# Revit family: Sink-Bathroom_Vessel-KOHLER-Sartorial-K-75749
name_source: partatom
category: Plumbing Fixtures
revit_build: Autodesk Revit 2015 (Build: 20140606_1530(x64)
units: mm (PartAtom-declared; Revit-internal decimal feet)

## types (4) — shared parameters
ADA Compliant = Yes
Assembly Code = D2010400
CW Connection = No
Cold Water Inlet = Cold Water Inlet
Date Modified = 11/19/2018
Default Elevation = 34"
Drain Included = No
HW Connection = No
Height = 6 1/8"
Hot Water Inlet = Hot Water Inlet
Length = 21 1/8"
Manufacturer = KOHLER Co.
MasterFormat 1995 = 15410
MasterFormat 2004 = 22.41.16
Material = Vitreous China
Product Documentation Link = http://www.us.kohler.com
Product Name = Sartorial
Product Page URL = http://www.us.kohler.com
URL = https://www.us.kohler.com
Vent Connection = No
Waste Connection = Yes
Waste Water Outlet = Waste Water Outlet
Width = 14 9/16"

## per-type parameters (varying)
| type | Description | Finish | Model | Type |
| Herringbone, 0-White | Herringbone in White on Carillon Rectangle Wading Pool bathroom sink | Kohler-Vitreous_China-0-White | K-75749-HD1-0 | 1 |
| Paisley, 0-White | Paisley in White on Carillon Rectangle Wading Pool bathroom sink | Kohler-Vitreous_China-0-White | K-75749-FP1-0 | 2 |
| Paisley, 7-Black Black | Paisley in Black Black on Carillon Rectangle Wading Pool bathroom sink | Kohler-Vitreous_China-7-Black_Black | K-75749-FP2-7 | 3 |
| Herringbone, 7-Black Black | Herringbone in Black Black on Carillon Rectangle Wading Pool bathroom sink | Kohler-Vitreous_China-7-Black_Black | K-75749-HD2-7 | 4 |

## geometry (parser evidence)
native form markers: Sweep x2
no freeform markers — native parametric forms only
